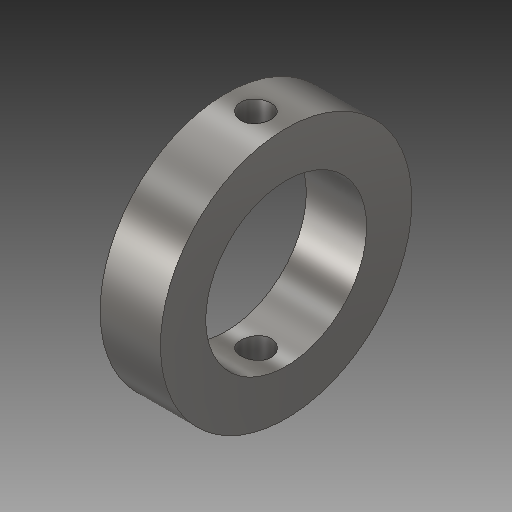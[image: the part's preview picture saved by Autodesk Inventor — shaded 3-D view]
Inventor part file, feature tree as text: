
AUTODESK INVENTOR PART (.ipt)
format: ipt  version: 2018 (Build 220112000, 112)  size: 137,728 bytes
history: native  units: mm
features: extrude x2, sketch x2, plane x1
ambient origin geometry x8: Origin, YZ Plane, XZ Plane, XY Plane, X Axis, Y Axis, Z Axis, Center Point
bodies: Solid1 (feature_tree)
feature tree (5):
  extrude  "Extrusion1"  Depth=32.0mm
  plane  "Work Plane1"
  extrude  "Extrusion2"  Depth=6.0mm
  sketch  "Sketch1"  dims[d0=50.0mm d1=32.0mm]
  sketch  "Sketch2"  dims[d2=12.0mm d3=0.0mm d4=6.0mm d5=12.0mm d6=0.0mm]
